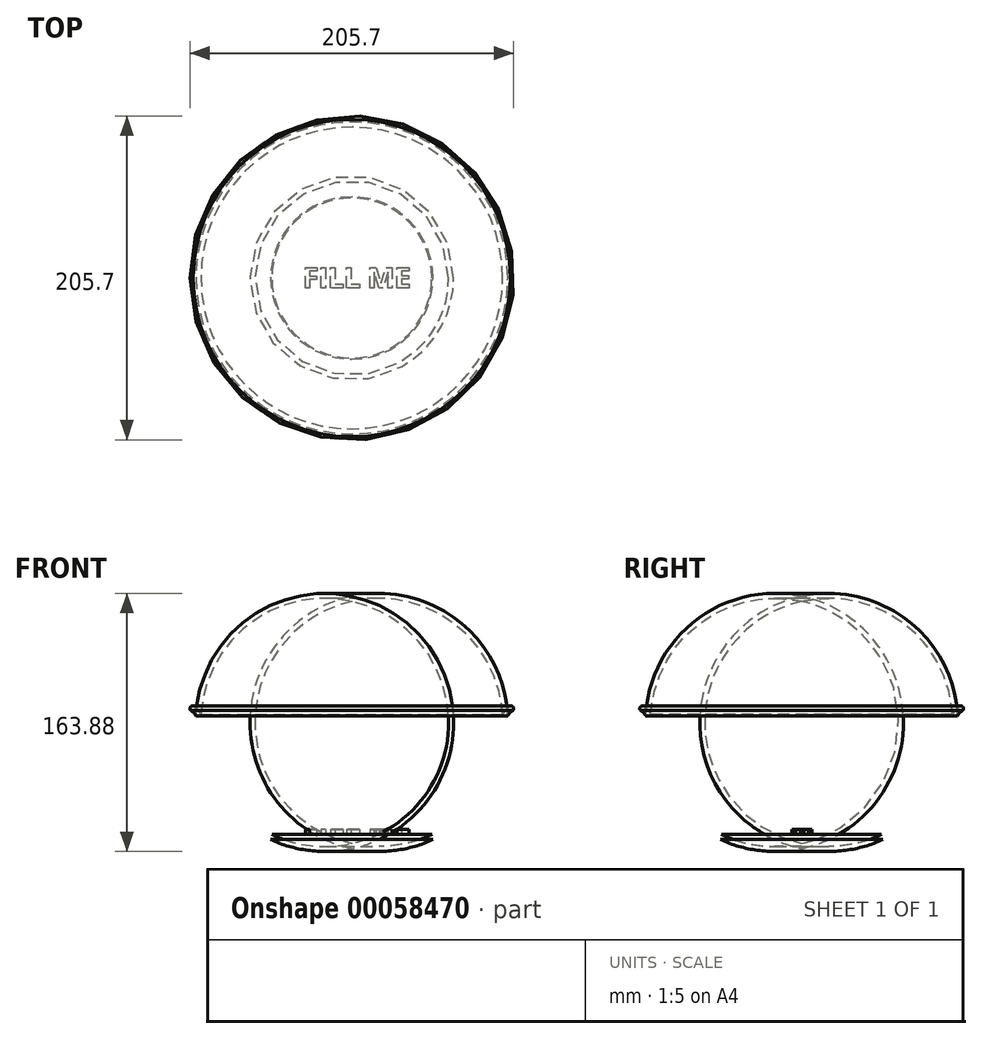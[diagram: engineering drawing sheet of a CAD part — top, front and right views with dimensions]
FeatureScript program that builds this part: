
annotation { "Feature Type Name" : "Feature", "Feature Type Description" : "" }
export const myFeature = defineFeature(function(context is Context, id is Id, definition is map)
    precondition{}
    {
        {
            var Q0;
            Q0=qCreatedBy(makeId("Front.planeOp"),FACE);
            var sketch = newSketch(context, id + "F0", { "sketchPlane" : qUnion([Q0])});
            skArc(sketch, "E0", {"start": v(-45.04, 76.2) * mm, "mid": v(-34.24, 31.18) * mm, "end": v(0, 0) * mm});
            skArc(sketch, "E1", {"start": v(-45.04, 76.2) * mm, "mid": v(-47.1, 79.29) * mm, "end": v(-49.97, 81.64) * mm});
            skLineSegment(sketch, "E2", {"start": v(0, 0) * mm, "end": v(50.8, 0) * mm});
            skArc(sketch, "E3.0", {"start": v(-48.26, 75.51) * mm, "mid": v(-49.71, 77.43) * mm, "end": v(-51.6, 78.92) * mm});
            skArc(sketch, "E3.1", {"start": v(-48.26, 75.51) * mm, "mid": v(-36.56, 28.87) * mm, "end": v(-0.7, -3.18) * mm});
            skLineSegment(sketch, "E3.2", {"start": v(-0.7, -3.18) * mm, "end": v(50.8, -3.18) * mm});
            skArc(sketch, "E4", {"start": v(-49.97, 81.64) * mm, "mid": v(-51.81, 80.9) * mm, "end": v(-51.6, 78.92) * mm});
            skLineSegment(sketch, "E5", {"start": v(50.8, -3.18) * mm, "end": v(50.8, 0) * mm});
            skSolve(sketch);
        }
        {
            var Q0;
            Q0 = qSketchRegion(id + "F0", true);
            var Q1;
            Q1=sQuery(id+"F0.wireOp",EDGE,"E5");
            revolve(context, id + "F1", {"entities" : qUnion([Q0]), "axis" : qUnion([Q1]), "revolveType" : RevolveType.FULL});
        }
        {
            var Q0;
            Q0=makeQuery(id+"F1.opRevolve","SWEPT_FACE",FACE,{"disambiguationData":[OSD([sQuery(id+"F0.wireOp",EDGE,"E2")])]});
            var sketch = newSketch(context, id + "F2", { "sketchPlane" : qUnion([Q0])});
            skText(sketch, "E6", { "text": "FILL ME", "fontName": "OpenSans-Bold.ttf"});
            const initialGuessF2  = {"E6": [0.01968, -0.00625, 1, 0, 0.01307]};
            skSetInitialGuess(sketch, initialGuessF2);
            skSolve(sketch);
        }
        {
            var Q0;
            Q0 = qSketchRegion(id + "F2", true);
            extrude(context, id + "F3", {"entities" : qUnion([Q0]), "operationType" : NewBodyOperationType.ADD, "depth" : 3.17 * mm});
        }
    });
